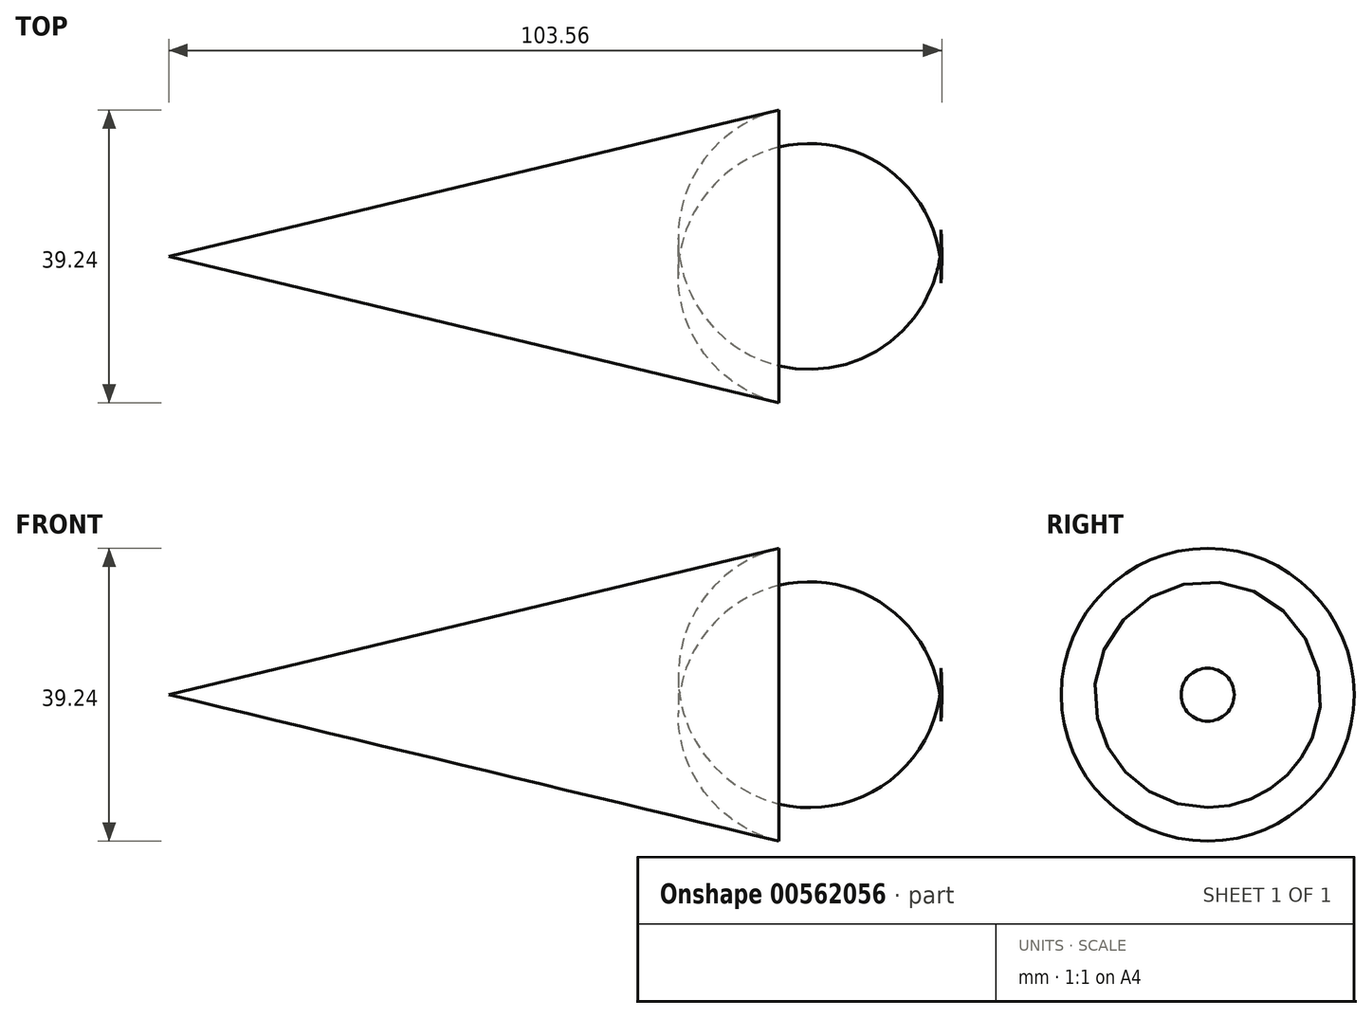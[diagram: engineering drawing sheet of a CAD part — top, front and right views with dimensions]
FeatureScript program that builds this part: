
annotation { "Feature Type Name" : "Feature", "Feature Type Description" : "" }
export const myFeature = defineFeature(function(context is Context, id is Id, definition is map)
    precondition{}
    {
        {
            var Q0;
            Q0=qCreatedBy(makeId("Top.planeOp"),FACE);
            var sketch = newSketch(context, id + "F0", { "sketchPlane" : qUnion([Q0])});
            skLineSegment(sketch, "E0", {"start": v(33.24, 23.65) * mm, "end": v(-65.34, 0) * mm});
            skArc(sketch, "E1", {"start": v(38.22, 0) * mm, "mid": v(36.96, 12.09) * mm, "end": v(33.24, 23.65) * mm});
            skPoint(sketch, "E2.center.orphan", {"position": v(38.06, 0) * mm});
            skLineSegment(sketch, "E3", {"start": v(-65.34, 0) * mm, "end": v(50, 0) * mm});
            skSolve(sketch);
        }
        {
            var Q0;
            {var subQ0=sQuery(id+"F0.wireOp",EDGE,"E0");Q0=makeQuery(id+"F0.imprint","IMPRINT",FACE,{"disambiguationData":[TD([[makeQuery(id+"F0.imprint","IMPRINT",EDGE,{"derivedFrom":subQ0}),1.0]])]});}
            var Q1;
            {var subQ0=sQuery(id+"F0.wireOp",EDGE,"P2wI0oyS-24IT-Urv2-41ZT-PyLooMPAa4cB");Q1=makeQuery(id+"F0.imprint","IMPRINT",FACE,{"disambiguationData":[TD([[makeQuery(id+"F0.imprint","IMPRINT",EDGE,{"derivedFrom":subQ0}),1.0]])]});}
            var Q2;
            Q2=sQuery(id+"F0.wireOp",EDGE,"E0");
            var Q3;
            Q3=sQuery(id+"F0.wireOp",EDGE,"E3");
            revolve(context, id + "F1", {"entities" : qUnion([Q0, Q1]), "surfaceEntities" : qUnion([Q2]), "axis" : qUnion([Q3]), "revolveType" : RevolveType.FULL});
        }
        {
            var Q0;
            Q0=makeQuery(id+"F1.opRevolve","SWEPT_EDGE",EDGE,{"disambiguationData":[OSD([sQuery(id+"F0.wireOp",EDGE,"E0"),sQuery(id+"F0.wireOp",EDGE,"E1")])]});
            fillet(context, id + "F2", {"entities" : qUnion([Q0]), "radius" : 17.62 * mm, "tangentPropagation" : true, "allowEdgeOverflow" : false});
        }
    });
